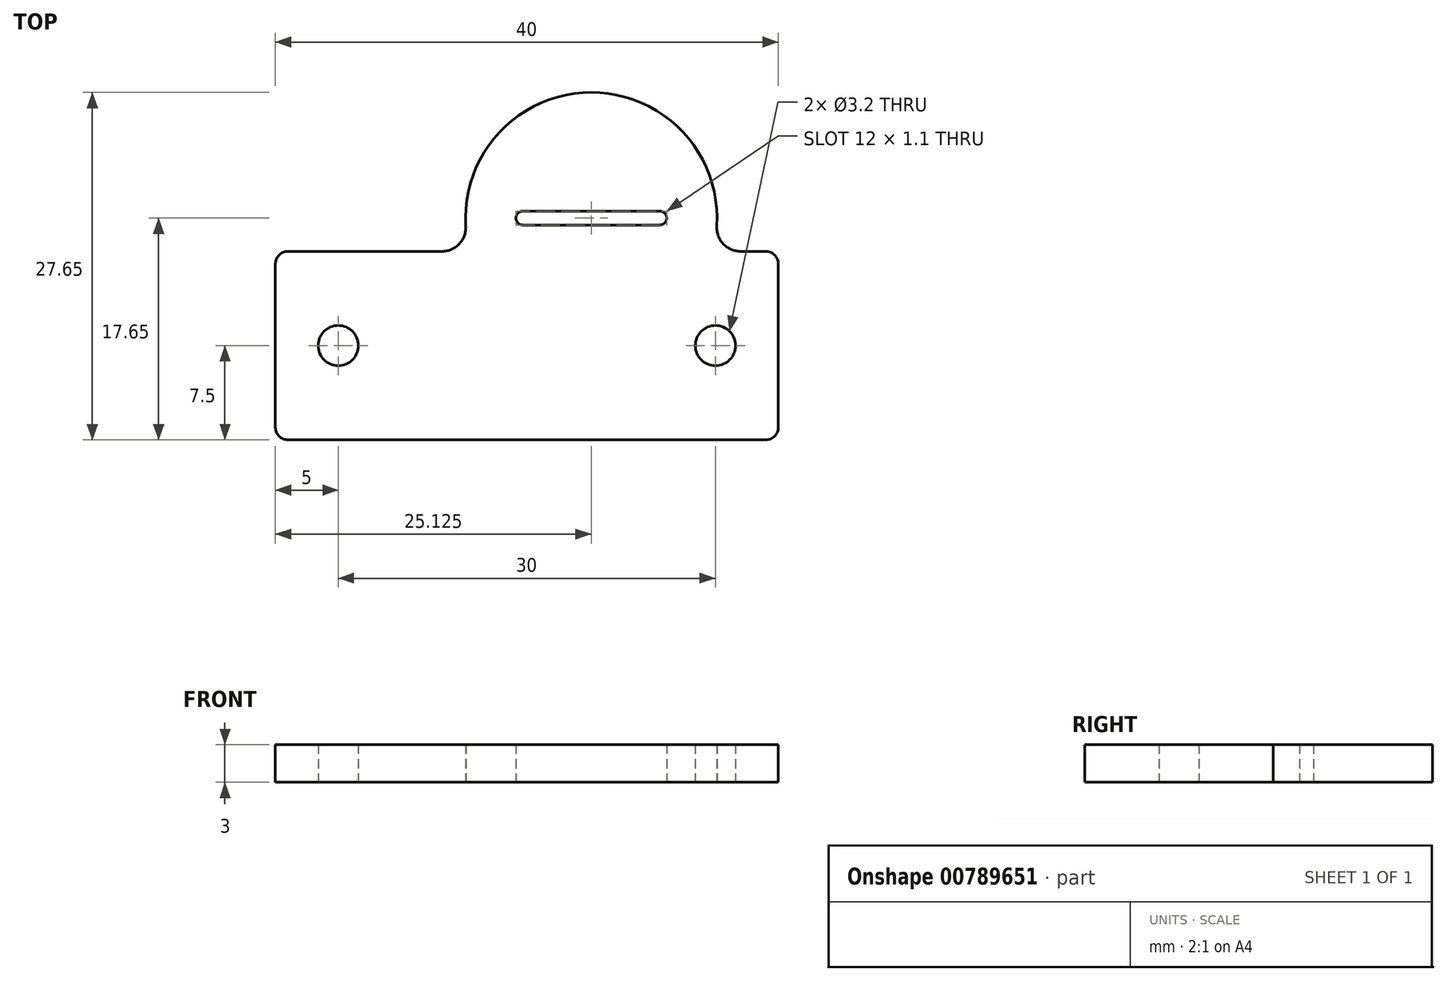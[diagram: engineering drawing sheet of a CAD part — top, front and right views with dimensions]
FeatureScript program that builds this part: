
annotation { "Feature Type Name" : "Feature", "Feature Type Description" : "" }
export const myFeature = defineFeature(function(context is Context, id is Id, definition is map)
    precondition{}
    {
        {
            var Q0;
            Q0=qCreatedBy(makeId("Top.planeOp"),FACE);
            var sketch = newSketch(context, id + "F0", { "sketchPlane" : qUnion([Q0])});
            skLineSegment(sketch, "E0", {"start": v(0, 0) * mm, "end": v(-20, 0) * mm, "construction": true});
            skLineSegment(sketch, "E1", {"start": v(0, 0) * mm, "end": v(0, 11.6) * mm, "construction": true});
            skLineSegment(sketch, "E2.MirrorCS", {"start": v(20, 7.5) * mm, "end": v(17, 7.5) * mm});
            skLineSegment(sketch, "E3.MirrorCS", {"start": v(20, -7.5) * mm, "end": v(-20, -7.5) * mm});
            skCircle(sketch, "E4", {"center": v(-15, 0) * mm, "radius": 1.6 * mm});
            skCircle(sketch, "E5.MirrorC", {"center": v(15, 0) * mm, "radius": 1.6 * mm});
            skCircle(sketch, "E6", {"center": v(5.13, 10.15) * mm, "radius": 6 * mm, "construction": true});
            skPoint(sketch, "E7.visualSharp", {"position": v(4.24, 7.5) * mm});
            skLineSegment(sketch, "E8", {"start": v(-20, 7.5) * mm, "end": v(-6.75, 7.5) * mm});
            skArc(sketch, "E9", {"start": v(15.1, 9.52) * mm, "mid": v(5.13, 20.15) * mm, "end": v(-4.86, 9.52) * mm});
            skPoint(sketch, "E10.visualSharp", {"position": v(-1.05, 7.5) * mm});
            skArc(sketch, "E10.filletArc", {"start": v(-6.75, 7.5) * mm, "mid": v(-5.37, 8.1) * mm, "end": v(-4.86, 9.52) * mm});
            skPoint(sketch, "E11.visualSharp", {"position": v(13.56, 7.5) * mm});
            skArc(sketch, "E11.filletArc", {"start": v(15.1, 9.52) * mm, "mid": v(15.62, 8.1) * mm, "end": v(17, 7.5) * mm});
            skLineSegment(sketch, "E12", {"start": v(-4.86, 9.52) * mm, "end": v(15.1, 9.52) * mm, "construction": true});
            skLineSegment(sketch, "E13.trimOffspring", {"start": v(-20, 7.5) * mm, "end": v(-20, 0) * mm});
            skLineSegment(sketch, "E14.trimOffspring", {"start": v(-20, -7.5) * mm, "end": v(-20, 0) * mm});
            skLineSegment(sketch, "E15.trimOffspring", {"start": v(20, -7.5) * mm, "end": v(20, 0) * mm});
            skLineSegment(sketch, "E16.trimOffspring", {"start": v(20, 7.5) * mm, "end": v(20, 0) * mm});
            skCircle(sketch, "E17", {"center": v(15, 0) * mm, "radius": 3 * mm, "construction": true});
            skCircle(sketch, "E18", {"center": v(-15, 0) * mm, "radius": 3 * mm, "construction": true});
            skLineSegment(sketch, "E19", {"start": v(-0.32, 10.15) * mm, "end": v(10.58, 10.15) * mm, "construction": true});
            skCircle(sketch, "E20", {"center": v(-0.32, 10.15) * mm, "radius": 0.55 * mm});
            skCircle(sketch, "E21", {"center": v(10.58, 10.15) * mm, "radius": 0.55 * mm});
            skLineSegment(sketch, "E22.bottom", {"start": v(-0.32, 10.7) * mm, "end": v(10.58, 10.7) * mm});
            skLineSegment(sketch, "E22.top", {"start": v(-0.32, 9.6) * mm, "end": v(10.58, 9.6) * mm});
            skLineSegment(sketch, "E22.left", {"start": v(-0.32, 10.7) * mm, "end": v(-0.32, 9.6) * mm, "construction": true});
            skLineSegment(sketch, "E22.right", {"start": v(10.58, 10.7) * mm, "end": v(10.58, 9.6) * mm, "construction": true});
            skSolve(sketch);
        }
        {
            var Q0;
            Q0=qSketchRegion(id+"F0",true);
            extrude(context, id + "F1", {"entities" : qUnion([Q0]), "depth" : 3 * mm, "offsetDistance" : 25 * mm});
        }
        {
            var Q0;
            Q0=makeQuery(id+"F1.opExtrude","SWEPT_EDGE",EDGE,{"disambiguationData":[OSD([sQuery(id+"F0.wireOp",EDGE,"E3.MirrorCS"),sQuery(id+"F0.wireOp",EDGE,"E14.trimOffspring")])]});
            var Q1;
            Q1=makeQuery(id+"F1.opExtrude","SWEPT_EDGE",EDGE,{"disambiguationData":[OSD([sQuery(id+"F0.wireOp",EDGE,"E3.MirrorCS"),sQuery(id+"F0.wireOp",EDGE,"E15.trimOffspring")])]});
            var Q2;
            Q2=makeQuery(id+"F1.opExtrude","SWEPT_EDGE",EDGE,{"disambiguationData":[OSD([sQuery(id+"F0.wireOp",EDGE,"E2.MirrorCS"),sQuery(id+"F0.wireOp",EDGE,"E16.trimOffspring")])]});
            var Q3;
            Q3=makeQuery(id+"F1.opExtrude","SWEPT_EDGE",EDGE,{"disambiguationData":[OSD([sQuery(id+"F0.wireOp",EDGE,"E8"),sQuery(id+"F0.wireOp",EDGE,"E13.trimOffspring")])]});
            fillet(context, id + "F2", {"entities" : qUnion([Q0, Q1, Q2, Q3]), "radius" : 1 * mm, "tangentPropagation" : true, "allowEdgeOverflow" : false});
        }
    });
